# Revit family: 63_LF_UN_Signify Trueline Suspended L1130 POE_IVLB
name_source: partatom
category: Lighting Fixtures
revit_build: Autodesk Revit 2017 (Build: 20190508_0315(x64)
units: mm (PartAtom-declared; Revit-internal decimal feet)

## family parameters
Always vertical = No
Cut with Voids When Loaded = No
Light Source = No
Part Type = Normal
Room Calculation Point = No
Round Connector Dimension = Use Diameter
Shared = No
Work Plane-Based = No

## types (2) — shared parameters
Apparent Load = 0 VA
Assembly Code = 63.0
Description = Geometry copy of fixture
Family Instance = EURS_63_LF_FB_TrueLine suspended SP530P SP531P SP532P SP533P L1130 POE_PHI : SP530P L1130 1 xLED15S_830 OC
IfcExportAs = IfcLightFixtureType
IfcExportType = USERDEFINED
Model = Generic Geometry
Rotation XZ Axis = 0.00°
Rotation YZ Axis = 0.00°
Type Comments = Unhosted - IVLibrary

## type names (no varying parameters)
- Costumizable ll Family Instance
- 63_LF_UN_Signify Trueline Suspended L1130 POE_IVLB

## geometry (parser evidence)
native form markers: Sweep x24
no freeform markers — native parametric forms only
